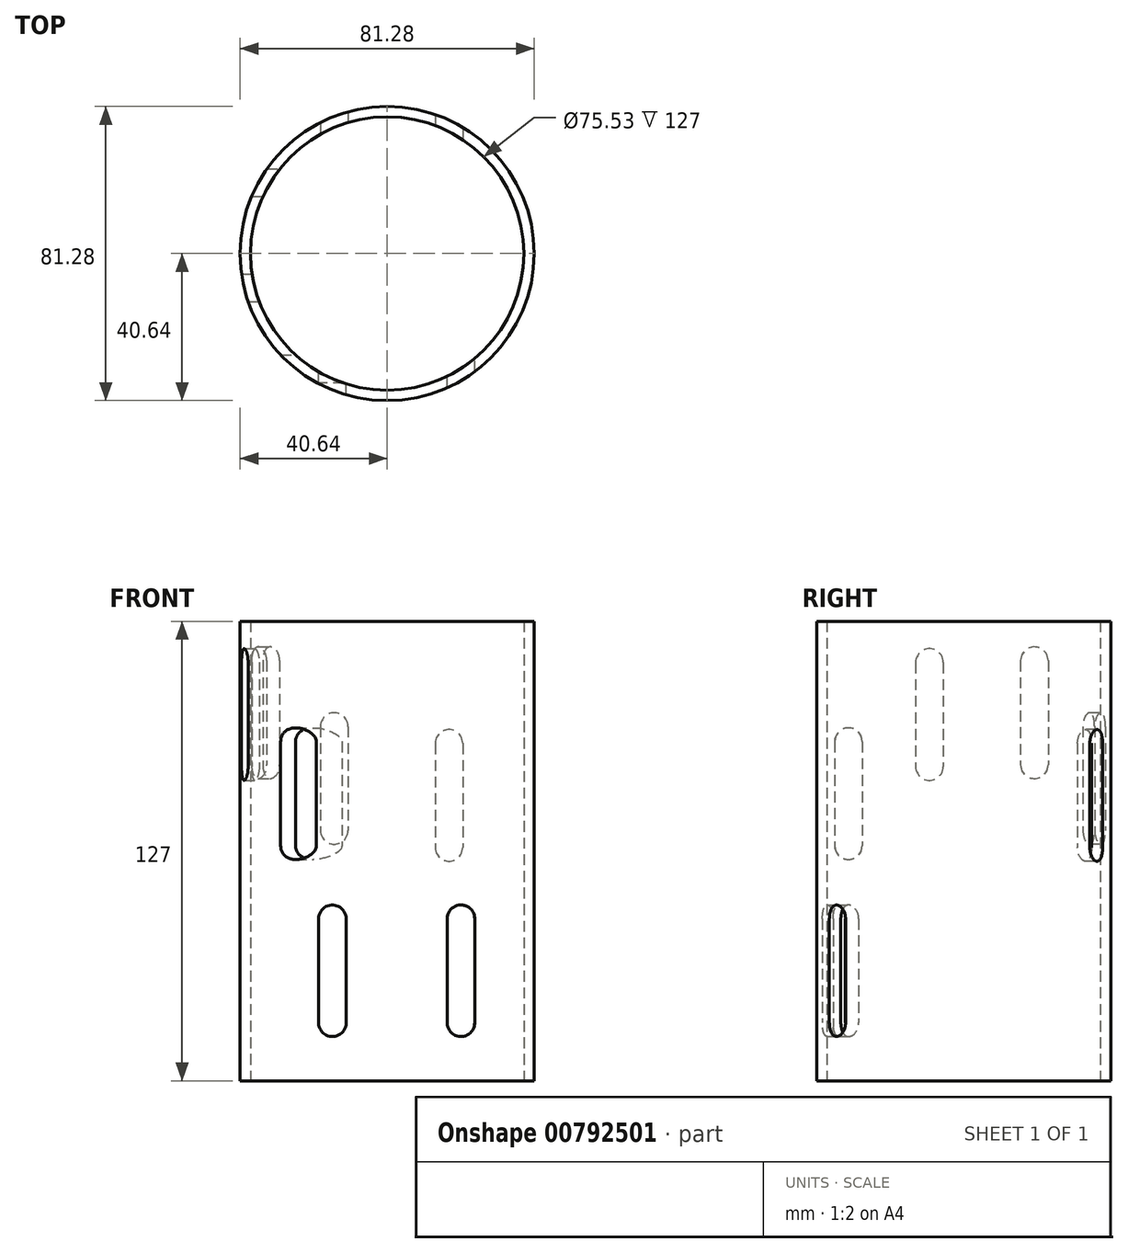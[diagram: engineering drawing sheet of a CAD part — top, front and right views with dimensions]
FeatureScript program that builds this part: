
annotation { "Feature Type Name" : "Feature", "Feature Type Description" : "" }
export const myFeature = defineFeature(function(context is Context, id is Id, definition is map)
    precondition{}
    {
        {
            var Q0;
            Q0=qCreatedBy(makeId("Top.planeOp"),FACE);
            var sketch = newSketch(context, id + "F0", { "sketchPlane" : qUnion([Q0])});
            skCircle(sketch, "E0", {"center": v(0, 0) * mm, "radius": 40.64 * mm});
            skCircle(sketch, "E1", {"center": v(0, 0) * mm, "radius": 37.77 * mm});
            skSolve(sketch);
        }
        {
            var Q0;
            Q0=makeQuery(id+"F0.imprint","IMPRINT",FACE,{"disambiguationData":[TD([[makeQuery(id+"F0.imprint","IMPRINT",EDGE,{"derivedFrom":sQuery(id+"F0.wireOp",EDGE,"E0")}),1.0]])]});
            extrude(context, id + "F1", {"entities" : qUnion([Q0]), "depth" : 127 * mm, "offsetDistance" : 25.4 * mm});
        }
        {
            var Q0;
            Q0=qCreatedBy(makeId("Front.planeOp"),FACE);
            var sketch = newSketch(context, id + "F2", { "sketchPlane" : qUnion([Q0])});
            skLineSegment(sketch, "E2.left", {"start": v(16.6, 44.78) * mm, "end": v(16.6, 16.02) * mm});
            skLineSegment(sketch, "E2.right", {"start": v(24.21, 44.78) * mm, "end": v(24.21, 16.02) * mm});
            skArc(sketch, "E3", {"start": v(24.21, 44.78) * mm, "mid": v(20.4, 48.6) * mm, "end": v(16.6, 44.78) * mm});
            skArc(sketch, "E4", {"start": v(16.6, 16.02) * mm, "mid": v(20.4, 12.21) * mm, "end": v(24.21, 16.02) * mm});
            skLineSegment(sketch, "E5.left", {"start": v(-18.93, 44.78) * mm, "end": v(-18.93, 16.02) * mm});
            skLineSegment(sketch, "E5.right", {"start": v(-11.3, 44.78) * mm, "end": v(-11.3, 16.02) * mm});
            skArc(sketch, "E6", {"start": v(-11.3, 44.78) * mm, "mid": v(-15.12, 48.6) * mm, "end": v(-18.93, 44.78) * mm});
            skArc(sketch, "E7", {"start": v(-18.93, 16.02) * mm, "mid": v(-15.12, 12.21) * mm, "end": v(-11.3, 16.02) * mm});
            skLineSegment(sketch, "E8.left", {"start": v(13.27, 93.25) * mm, "end": v(13.27, 64.5) * mm});
            skLineSegment(sketch, "E8.right", {"start": v(20.9, 93.25) * mm, "end": v(20.9, 64.5) * mm});
            skArc(sketch, "E9", {"start": v(20.9, 93.25) * mm, "mid": v(17.08, 97.06) * mm, "end": v(13.27, 93.25) * mm});
            skArc(sketch, "E10", {"start": v(13.27, 64.5) * mm, "mid": v(17.08, 60.68) * mm, "end": v(20.9, 64.5) * mm});
            skLineSegment(sketch, "E11.left", {"start": v(-18.44, 97.93) * mm, "end": v(-18.44, 69.17) * mm});
            skLineSegment(sketch, "E11.right", {"start": v(-10.82, 97.93) * mm, "end": v(-10.82, 69.17) * mm});
            skArc(sketch, "E12", {"start": v(-10.82, 97.93) * mm, "mid": v(-14.63, 101.74) * mm, "end": v(-18.44, 97.93) * mm});
            skArc(sketch, "E13", {"start": v(-18.44, 69.17) * mm, "mid": v(-14.63, 65.36) * mm, "end": v(-10.82, 69.17) * mm});
            skLineSegment(sketch, "E14", {"start": v(20.4, 12.21) * mm, "end": v(-27.4, 12.21) * mm});
            skSolve(sketch);
        }
        {
            var Q0;
            Q0=makeQuery(id+"F2.imprint","IMPRINT",FACE,{"disambiguationData":[TD([[makeQuery(id+"F2.imprint","IMPRINT",EDGE,{"derivedFrom":sQuery(id+"F2.wireOp",EDGE,"E8.left")}),1.0]])]});
            extrude(context, id + "F3", {"entities" : qUnion([Q0]), "operationType" : NewBodyOperationType.REMOVE, "endBound" : BoundingType.THROUGH_ALL, "oppositeDirection" : true, "depth" : 25.4 * mm, "offsetDistance" : 25.4 * mm});
        }
        {
            var Q0;
            Q0=makeQuery(id+"F2.imprint","IMPRINT",FACE,{"disambiguationData":[TD([[makeQuery(id+"F2.imprint","IMPRINT",EDGE,{"derivedFrom":sQuery(id+"F2.wireOp",EDGE,"E11.left")}),1.0]])]});
            extrude(context, id + "F4", {"entities" : qUnion([Q0]), "operationType" : NewBodyOperationType.REMOVE, "oppositeDirection" : true, "depth" : 76.2 * mm, "offsetDistance" : 25.4 * mm});
        }
        {
            var Q0;
            {var subQ0=sQuery(id+"F2.wireOp",EDGE,"E5.left");Q0=makeQuery(id+"F2.imprint","IMPRINT",FACE,{"disambiguationData":[TD([[makeQuery(id+"F2.imprint","IMPRINT",EDGE,{"derivedFrom":subQ0}),1.0]])]});}
            extrude(context, id + "F5", {"entities" : qUnion([Q0]), "operationType" : NewBodyOperationType.REMOVE, "depth" : 50.8 * mm, "offsetDistance" : 25.4 * mm});
        }
        {
            var Q0;
            {var subQ1=sQuery(id+"F2.wireOp",EDGE,"E2.left");Q0=makeQuery(id+"F2.imprint","IMPRINT",FACE,{"disambiguationData":[TD([[makeQuery(id+"F2.imprint","IMPRINT",EDGE,{"derivedFrom":subQ1}),1.0]])]});}
            extrude(context, id + "F6", {"entities" : qUnion([Q0]), "operationType" : NewBodyOperationType.REMOVE, "depth" : 50.8 * mm, "offsetDistance" : 25.4 * mm});
        }
        {
            var Q0;
            Q0=qCreatedBy(makeId("Right.planeOp"),FACE);
            var sketch = newSketch(context, id + "F7", { "sketchPlane" : qUnion([Q0])});
            skLineSegment(sketch, "E15.left", {"start": v(-35.64, 93.73) * mm, "end": v(-35.64, 64.97) * mm});
            skLineSegment(sketch, "E15.right", {"start": v(-28.02, 93.73) * mm, "end": v(-28.02, 64.97) * mm});
            skArc(sketch, "E16", {"start": v(-28.02, 93.73) * mm, "mid": v(-31.83, 97.54) * mm, "end": v(-35.64, 93.73) * mm});
            skArc(sketch, "E17", {"start": v(-35.64, 64.97) * mm, "mid": v(-31.83, 61.16) * mm, "end": v(-28.02, 64.97) * mm});
            skLineSegment(sketch, "E18.left", {"start": v(15.73, 116.1) * mm, "end": v(15.73, 87.34) * mm});
            skLineSegment(sketch, "E18.right", {"start": v(23.35, 116.1) * mm, "end": v(23.35, 87.34) * mm});
            skArc(sketch, "E19", {"start": v(23.35, 116.1) * mm, "mid": v(19.54, 119.91) * mm, "end": v(15.73, 116.1) * mm});
            skArc(sketch, "E20", {"start": v(15.73, 87.34) * mm, "mid": v(19.54, 83.53) * mm, "end": v(23.35, 87.34) * mm});
            skLineSegment(sketch, "E21.left", {"start": v(-13.27, 115.61) * mm, "end": v(-13.27, 86.85) * mm});
            skLineSegment(sketch, "E21.right", {"start": v(-5.65, 115.61) * mm, "end": v(-5.65, 86.85) * mm});
            skArc(sketch, "E22", {"start": v(-5.65, 115.61) * mm, "mid": v(-9.46, 119.42) * mm, "end": v(-13.27, 115.61) * mm});
            skArc(sketch, "E23", {"start": v(-13.27, 86.85) * mm, "mid": v(-9.46, 83.04) * mm, "end": v(-5.65, 86.85) * mm});
            skLineSegment(sketch, "E24.left", {"start": v(26.55, 37.7) * mm, "end": v(26.55, 8.93) * mm});
            skLineSegment(sketch, "E24.right", {"start": v(34.17, 37.7) * mm, "end": v(34.17, 8.93) * mm});
            skArc(sketch, "E25", {"start": v(34.17, 37.7) * mm, "mid": v(30.36, 41.5) * mm, "end": v(26.55, 37.7) * mm});
            skArc(sketch, "E26", {"start": v(26.55, 8.93) * mm, "mid": v(30.36, 5.12) * mm, "end": v(34.17, 8.93) * mm});
            skLineSegment(sketch, "E27.left", {"start": v(-11.06, 44.82) * mm, "end": v(-11.06, 16.06) * mm});
            skLineSegment(sketch, "E27.right", {"start": v(-3.44, 44.82) * mm, "end": v(-3.44, 16.06) * mm});
            skArc(sketch, "E28", {"start": v(-3.44, 44.82) * mm, "mid": v(-7.25, 48.63) * mm, "end": v(-11.06, 44.82) * mm});
            skArc(sketch, "E29", {"start": v(-11.06, 16.06) * mm, "mid": v(-7.25, 12.25) * mm, "end": v(-3.44, 16.06) * mm});
            skSolve(sketch);
        }
        {
            var Q0;
            Q0=makeQuery(id+"F7.imprint","IMPRINT",FACE,{"disambiguationData":[TD([[makeQuery(id+"F7.imprint","IMPRINT",EDGE,{"derivedFrom":sQuery(id+"F7.wireOp",EDGE,"E21.left")}),1.0]])]});
            extrude(context, id + "F8", {"entities" : qUnion([Q0]), "operationType" : NewBodyOperationType.REMOVE, "oppositeDirection" : true, "depth" : 50.8 * mm, "offsetDistance" : 25.4 * mm});
        }
        {
            var Q0;
            Q0=makeQuery(id+"F7.imprint","IMPRINT",FACE,{"disambiguationData":[TD([[makeQuery(id+"F7.imprint","IMPRINT",EDGE,{"derivedFrom":sQuery(id+"F7.wireOp",EDGE,"E21.left")}),1.0]])]});
            var Q1;
            Q1=makeQuery(id+"F7.imprint","IMPRINT",FACE,{"disambiguationData":[TD([[makeQuery(id+"F7.imprint","IMPRINT",EDGE,{"derivedFrom":sQuery(id+"F7.wireOp",EDGE,"E15.left")}),1.0]])]});
            var Q2;
            Q2=makeQuery(id+"F7.imprint","IMPRINT",FACE,{"disambiguationData":[TD([[makeQuery(id+"F7.imprint","IMPRINT",EDGE,{"derivedFrom":sQuery(id+"F7.wireOp",EDGE,"E18.left")}),1.0]])]});
            extrude(context, id + "F9", {"entities" : qUnion([Q0, Q1, Q2]), "operationType" : NewBodyOperationType.REMOVE, "oppositeDirection" : true, "depth" : 50.8 * mm, "offsetDistance" : 25.4 * mm});
        }
    });
